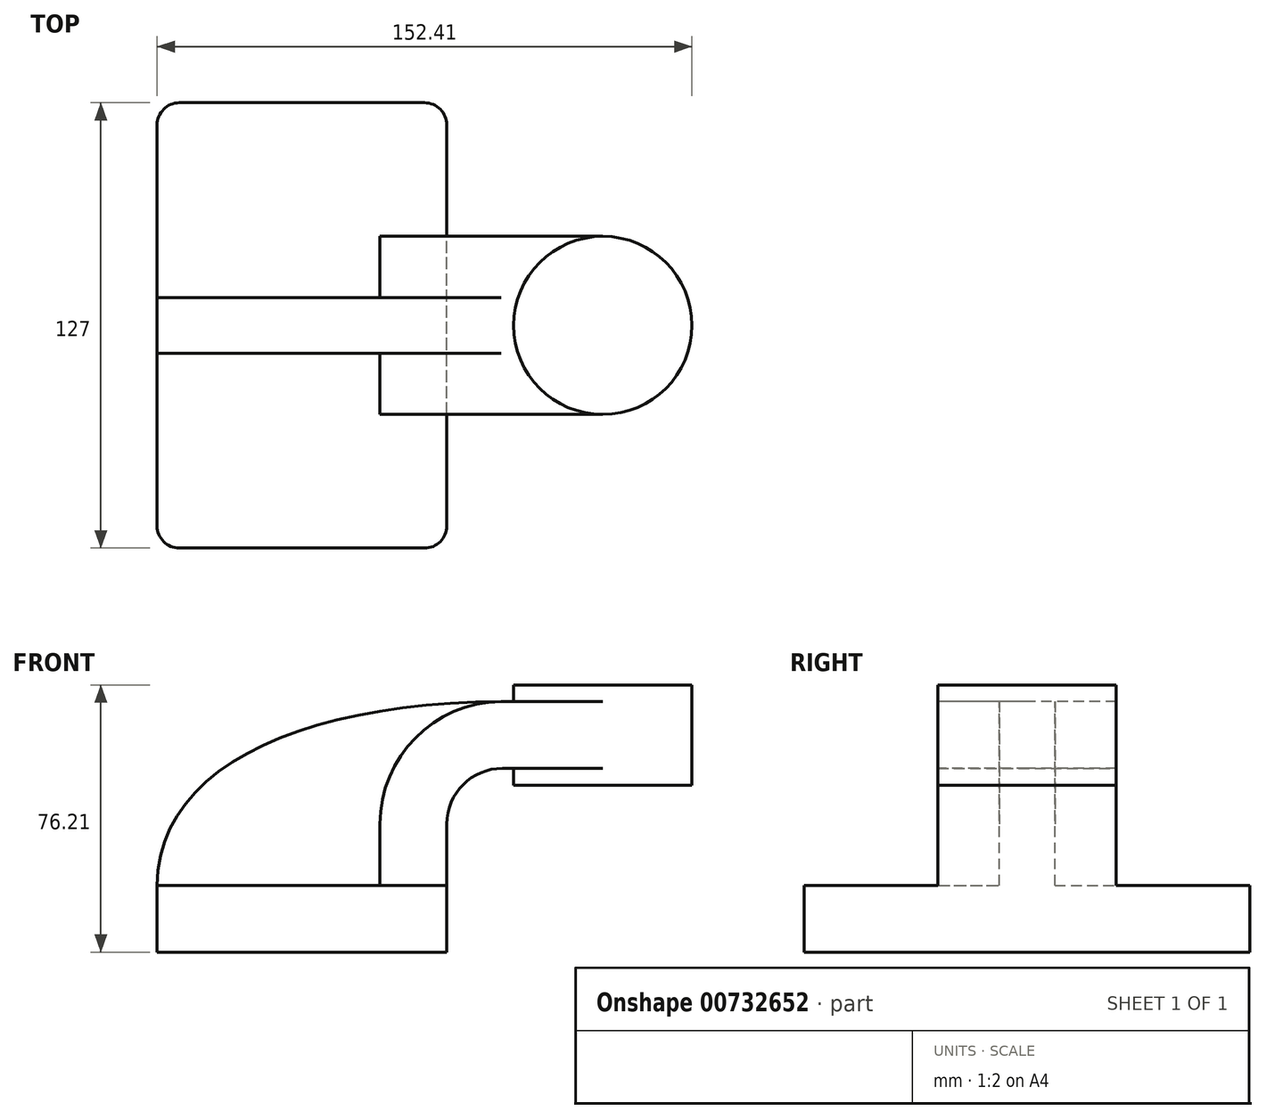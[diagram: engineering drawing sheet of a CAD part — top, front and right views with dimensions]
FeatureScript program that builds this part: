
annotation { "Feature Type Name" : "Feature", "Feature Type Description" : "" }
export const myFeature = defineFeature(function(context is Context, id is Id, definition is map)
    precondition{}
    {
        {
            var Q0;
            Q0=qCreatedBy(makeId("Front.planeOp"),FACE);
            var sketch = newSketch(context, id + "F0", { "sketchPlane" : qUnion([Q0])});
            skLineSegment(sketch, "E0.bottom", {"start": v(-41.28, 9.52) * mm, "end": v(41.27, 9.53) * mm});
            skLineSegment(sketch, "E0.top", {"start": v(-41.28, -9.52) * mm, "end": v(41.28, -9.52) * mm});
            skLineSegment(sketch, "E0.left", {"start": v(-41.28, 9.52) * mm, "end": v(-41.28, -9.53) * mm});
            skLineSegment(sketch, "E0.right", {"start": v(41.27, 9.53) * mm, "end": v(41.28, -9.52) * mm});
            skPoint(sketch, "E0.middle", {"position": v(0, 0) * mm});
            skLineSegment(sketch, "E1.bottom", {"start": v(60.33, 38.1) * mm, "end": v(111.12, 38.1) * mm});
            skLineSegment(sketch, "E1.top", {"start": v(60.33, 66.68) * mm, "end": v(111.12, 66.68) * mm});
            skLineSegment(sketch, "E1.left", {"start": v(60.33, 38.1) * mm, "end": v(60.32, 66.68) * mm});
            skLineSegment(sketch, "E1.right", {"start": v(111.12, 38.1) * mm, "end": v(111.12, 66.68) * mm});
            skPoint(sketch, "E1.middle", {"position": v(85.72, 52.39) * mm});
            skLineSegment(sketch, "E2", {"start": v(41.27, 9.53) * mm, "end": v(41.27, 27) * mm});
            skArc(sketch, "E3", {"start": v(41.27, 27) * mm, "mid": v(45.92, 38.23) * mm, "end": v(57.15, 42.88) * mm});
            skLineSegment(sketch, "E4", {"start": v(57.15, 42.88) * mm, "end": v(85.72, 42.88) * mm});
            skLineSegment(sketch, "E5.0", {"start": v(57.15, 61.93) * mm, "end": v(85.72, 61.93) * mm});
            skArc(sketch, "E5.1", {"start": v(22.22, 27) * mm, "mid": v(32.45, 51.7) * mm, "end": v(57.15, 61.93) * mm});
            skLineSegment(sketch, "E5.2", {"start": v(22.22, 9.53) * mm, "end": v(22.22, 27) * mm});
            skLineSegment(sketch, "E6", {"start": v(85.72, 38.1) * mm, "end": v(85.72, 66.68) * mm});
            skFitSpline(sketch, "E7", {"points": [v(-41.28, 9.52) * mm, v(57.15, 61.93) * mm], "startDerivative": vector(0.95, 101.6) * mm, "endDerivative": vector(171.45, 0.78) * mm});
            skSolve(sketch);
        }
        {
            var Q0;
            Q0=makeQuery(id+"F0.imprint","IMPRINT",FACE,{"disambiguationData":[TD([[makeQuery(id+"F0.imprint","IMPRINT",EDGE,{"derivedFrom":sQuery(id+"F0.wireOp",EDGE,"E0.top")}),1.0]])]});
            extrude(context, id + "F1", {"entities" : qUnion([Q0]), "endBound" : BoundingType.SYMMETRIC, "depth" : 127 * mm, "offsetDistance" : 25.4 * mm});
        }
        {
            var Q0;
            {var subQ1=sQuery(id+"F0.wireOp",EDGE,"E2");Q0=makeQuery(id+"F0.imprint","IMPRINT",FACE,{"disambiguationData":[TD([[makeQuery(id+"F0.imprint","IMPRINT",EDGE,{"derivedFrom":subQ1}),1.0]])]});}
            var Q1;
            {var subQ0=sQuery(id+"F0.wireOp",EDGE,"E4");var subQ1=sQuery(id+"F0.wireOp",EDGE,"E1.left");var subQ2=makeQuery(id+"F0.imprint","INTERSECT",VERTEX,{"derivedFrom":[subQ1,subQ0]});Q1=makeQuery(id+"F0.imprint","IMPRINT",FACE,{"disambiguationData":[TD([[makeQuery(id+"F0.imprint","IMPRINT",EDGE,{"disambiguationData":[TD([[subQ2,-1.0]])],"derivedFrom":subQ1}),-1.0]])]});}
            extrude(context, id + "F2", {"entities" : qUnion([Q0, Q1]), "operationType" : NewBodyOperationType.ADD, "endBound" : BoundingType.SYMMETRIC, "depth" : 50.8 * mm, "offsetDistance" : 25.4 * mm});
        }
        {
            var Q0;
            {var subQ3=sQuery(id+"F0.wireOp",EDGE,"E5.2");Q0=makeQuery(id+"F0.imprint","IMPRINT",FACE,{"disambiguationData":[TD([[makeQuery(id+"F0.imprint","IMPRINT",EDGE,{"derivedFrom":subQ3}),1.0]])]});}
            extrude(context, id + "F3", {"entities" : qUnion([Q0]), "operationType" : NewBodyOperationType.ADD, "endBound" : BoundingType.SYMMETRIC, "depth" : 15.88 * mm, "offsetDistance" : 25.4 * mm});
        }
        {
            var Q0;
            {var subQ4=sQuery(id+"F0.wireOp",EDGE,"E1.right");Q0=makeQuery(id+"F0.imprint","IMPRINT",FACE,{"disambiguationData":[TD([[makeQuery(id+"F0.imprint","IMPRINT",EDGE,{"derivedFrom":subQ4}),1.0]])]});}
            var Q1;
            Q1=sQuery(id+"F0.wireOp",EDGE,"E6");
            revolve(context, id + "F4", {"operationType" : NewBodyOperationType.ADD, "surfaceOperationType" : NewSurfaceOperationType.NEW, "entities" : qUnion([Q0]), "axis" : qUnion([Q1]), "revolveType" : RevolveType.FULL});
        }
        {
            var Q0;
            Q0=makeQuery(id+"F1.opExtrude","CAP_EDGE",EDGE,{"disambiguationData":[OSD([sQuery(id+"F0.wireOp",EDGE,"E0.left")])],"isStart":false});
            var Q1;
            Q1=makeQuery(id+"F1.opExtrude","CAP_EDGE",EDGE,{"disambiguationData":[OSD([sQuery(id+"F0.wireOp",EDGE,"E0.right")])],"isStart":false});
            var Q2;
            Q2=makeQuery(id+"F1.opExtrude","CAP_EDGE",EDGE,{"disambiguationData":[OSD([sQuery(id+"F0.wireOp",EDGE,"E0.right")])],"isStart":true});
            var Q3;
            Q3=makeQuery(id+"F1.opExtrude","CAP_EDGE",EDGE,{"disambiguationData":[OSD([sQuery(id+"F0.wireOp",EDGE,"E0.left")])],"isStart":true});
            fillet(context, id + "F5", {"entities" : qUnion([Q0, Q1, Q2, Q3]), "radius" : 6.35 * mm, "tangentPropagation" : true, "allowEdgeOverflow" : false});
        }
    });
